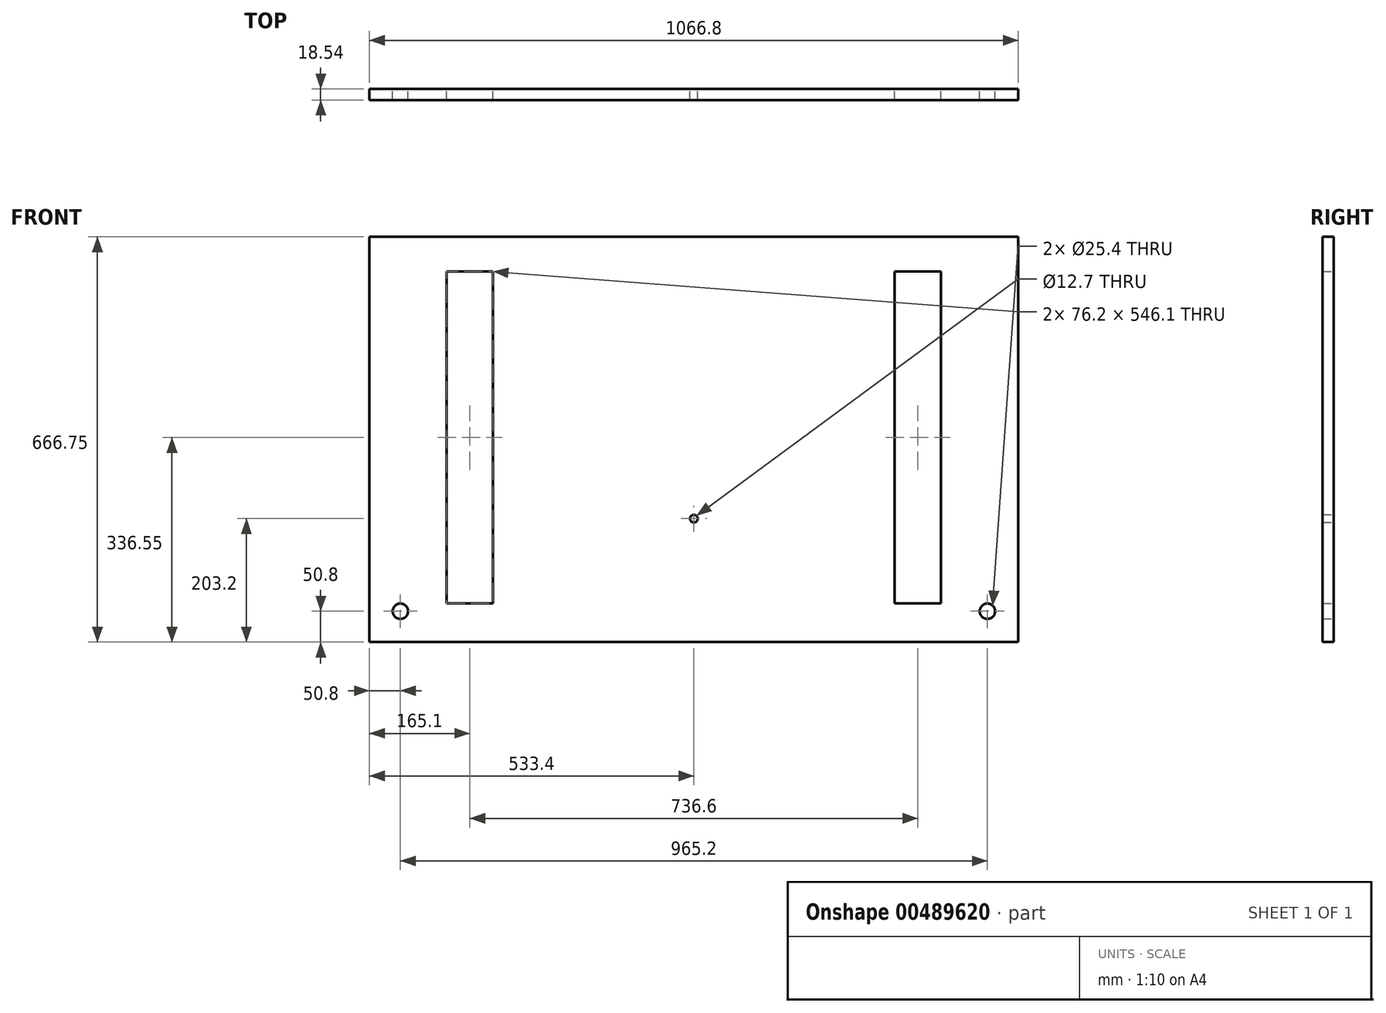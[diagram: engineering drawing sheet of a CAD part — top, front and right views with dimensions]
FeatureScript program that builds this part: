
annotation { "Feature Type Name" : "Feature", "Feature Type Description" : "" }
export const myFeature = defineFeature(function(context is Context, id is Id, definition is map)
    precondition{}
    {
        {
            var Q0;
            Q0=qCreatedBy(makeId("Front.planeOp"),FACE);
            var sketch = newSketch(context, id + "F0", { "sketchPlane" : qUnion([Q0])});
            skLineSegment(sketch, "E0.top", {"start": v(533.4, 336.55) * mm, "end": v(-533.4, 336.55) * mm});
            skLineSegment(sketch, "E0.left", {"start": v(533.4, -336.55) * mm, "end": v(533.4, 336.55) * mm});
            skLineSegment(sketch, "E0.right", {"start": v(-533.4, -336.55) * mm, "end": v(-533.4, 336.55) * mm});
            skPoint(sketch, "E0.middle", {"position": v(0, 0) * mm});
            skLineSegment(sketch, "E1.0", {"start": v(533.4, -330.2) * mm, "end": v(-533.4, -330.2) * mm});
            skLineSegment(sketch, "E2.bottom", {"start": v(406.4, -266.7) * mm, "end": v(330.2, -266.7) * mm});
            skLineSegment(sketch, "E2.top", {"start": v(406.4, 279.4) * mm, "end": v(330.2, 279.4) * mm});
            skLineSegment(sketch, "E2.left", {"start": v(406.4, -266.7) * mm, "end": v(406.4, 279.4) * mm});
            skLineSegment(sketch, "E2.right", {"start": v(330.2, -266.7) * mm, "end": v(330.2, 279.4) * mm});
            skLineSegment(sketch, "E3.bottom", {"start": v(-406.4, -266.7) * mm, "end": v(-330.2, -266.7) * mm});
            skLineSegment(sketch, "E3.top", {"start": v(-406.4, 279.4) * mm, "end": v(-330.2, 279.4) * mm});
            skLineSegment(sketch, "E3.left", {"start": v(-406.4, -266.7) * mm, "end": v(-406.4, 279.4) * mm});
            skLineSegment(sketch, "E3.right", {"start": v(-330.2, -266.7) * mm, "end": v(-330.2, 279.4) * mm});
            skCircle(sketch, "E4", {"center": v(0, -127) * mm, "radius": 6.35 * mm});
            skCircle(sketch, "E5", {"center": v(482.6, -279.4) * mm, "radius": 12.7 * mm});
            skCircle(sketch, "E6", {"center": v(-482.6, -279.4) * mm, "radius": 12.7 * mm});
            skSolve(sketch);
        }
        {
            var Q0;
            {var subQ0=sQuery(id+"F0.wireOp",EDGE,"E0.top");Q0=makeQuery(id+"F0.imprint","IMPRINT",FACE,{"disambiguationData":[TD([[makeQuery(id+"F0.imprint","IMPRINT",EDGE,{"derivedFrom":subQ0}),1.0]])]});}
            extrude(context, id + "F1", {"entities" : qUnion([Q0]), "depth" : 18.54 * mm, "offsetDistance" : 25.4 * mm});
        }
    });
